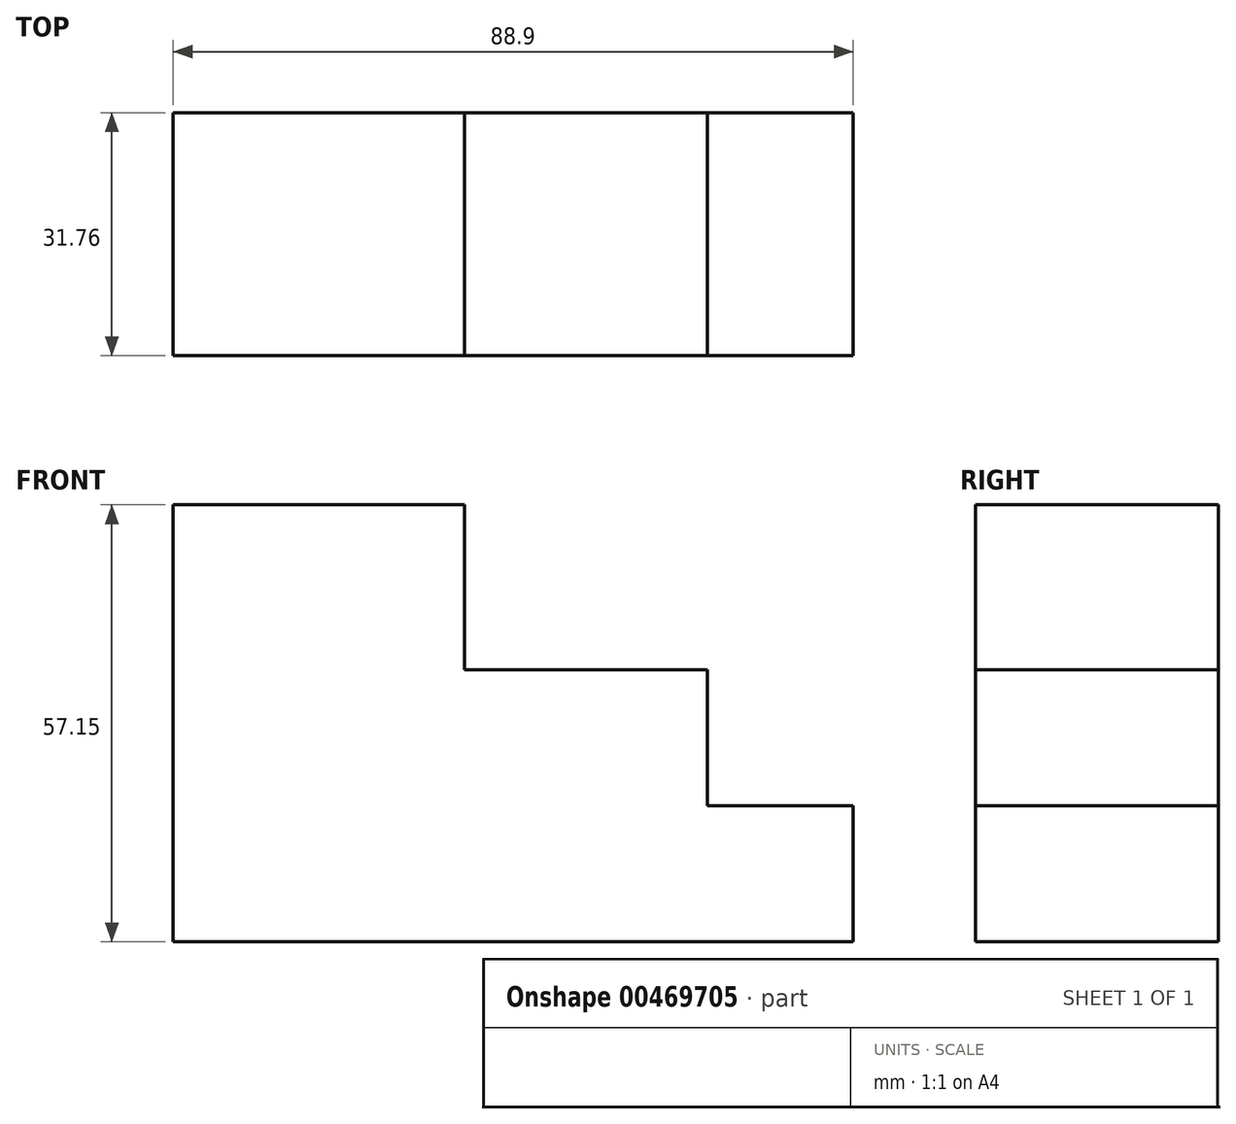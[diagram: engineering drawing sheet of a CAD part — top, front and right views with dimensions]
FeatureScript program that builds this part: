
annotation { "Feature Type Name" : "Feature", "Feature Type Description" : "" }
export const myFeature = defineFeature(function(context is Context, id is Id, definition is map)
    precondition{}
    {
        {
            var Q0;
            Q0=qCreatedBy(makeId("Front.planeOp"),FACE);
            var sketch = newSketch(context, id + "F0", { "sketchPlane" : qUnion([Q0])});
            skLineSegment(sketch, "E0.bottom", {"start": v(0, 0) * mm, "end": v(88.9, 0) * mm});
            skLineSegment(sketch, "E0.top", {"start": v(0, 57.15) * mm, "end": v(38.1, 57.15) * mm});
            skLineSegment(sketch, "E0.left", {"start": v(0, 0) * mm, "end": v(0, 57.15) * mm});
            skLineSegment(sketch, "E0.right", {"start": v(88.9, 0) * mm, "end": v(88.9, 17.78) * mm});
            skLineSegment(sketch, "E1.top", {"start": v(69.85, 35.56) * mm, "end": v(38.1, 35.56) * mm});
            skLineSegment(sketch, "E1.right", {"start": v(38.1, 57.15) * mm, "end": v(38.1, 35.56) * mm});
            skLineSegment(sketch, "E2.top", {"start": v(88.9, 17.78) * mm, "end": v(69.85, 17.78) * mm});
            skLineSegment(sketch, "E2.right", {"start": v(69.85, 35.56) * mm, "end": v(69.85, 17.78) * mm});
            skSolve(sketch);
        }
        {
            var Q0;
            Q0 = qSketchRegion(id + "F0", true);
            extrude(context, id + "F1", {"entities" : qUnion([Q0]), "endBound" : BoundingType.SYMMETRIC, "depth" : 31.75 * mm});
        }
    });
